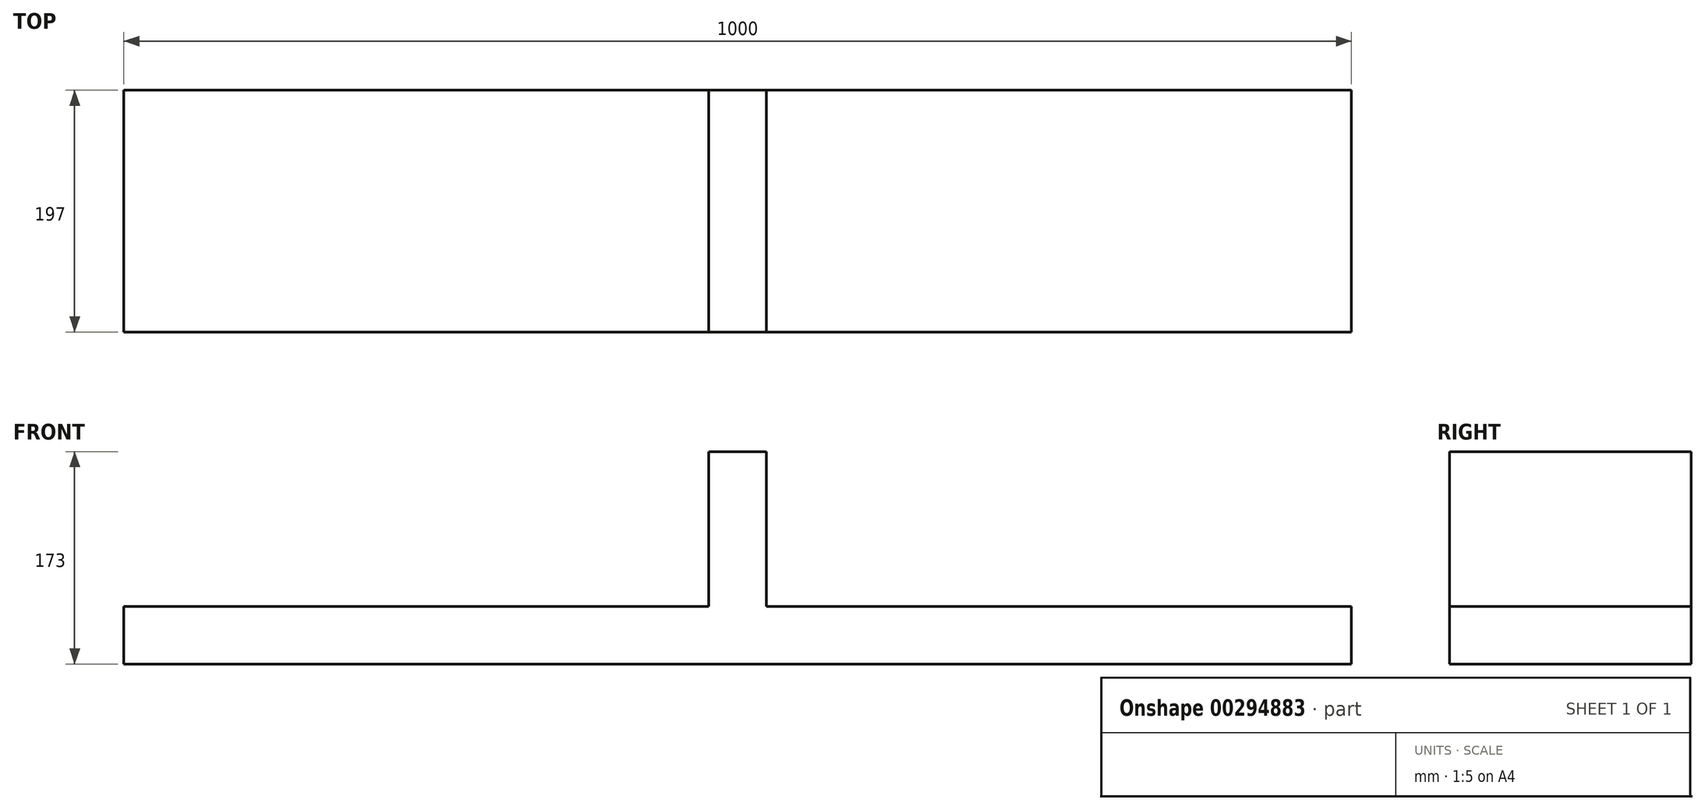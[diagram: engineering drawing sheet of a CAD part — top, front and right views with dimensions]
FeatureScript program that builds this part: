
annotation { "Feature Type Name" : "Feature", "Feature Type Description" : "" }
export const myFeature = defineFeature(function(context is Context, id is Id, definition is map)
    precondition{}
    {
        {
            var Q0;
            Q0=qCreatedBy(makeId("Front.planeOp"),FACE);
            var sketch = newSketch(context, id + "F0", { "sketchPlane" : qUnion([Q0])});
            skLineSegment(sketch, "E0", {"start": v(0, 173) * mm, "end": v(0, 0) * mm, "construction": true});
            skLineSegment(sketch, "E1", {"start": v(0, 0) * mm, "end": v(500, 0) * mm});
            skLineSegment(sketch, "E2", {"start": v(500, 0) * mm, "end": v(500, 47) * mm});
            skLineSegment(sketch, "E3", {"start": v(500, 47) * mm, "end": v(23.5, 47) * mm});
            skLineSegment(sketch, "E4", {"start": v(23.5, 47) * mm, "end": v(23.5, 173) * mm});
            skLineSegment(sketch, "E5", {"start": v(23.5, 173) * mm, "end": v(0, 173) * mm});
            skLineSegment(sketch, "E6.MirrorCS", {"start": v(-23.5, 173) * mm, "end": v(0, 173) * mm});
            skLineSegment(sketch, "E7.MirrorCS", {"start": v(-23.5, 47) * mm, "end": v(-23.5, 173) * mm});
            skLineSegment(sketch, "E8.MirrorCS", {"start": v(-500, 47) * mm, "end": v(-23.5, 47) * mm});
            skLineSegment(sketch, "E9.MirrorCS", {"start": v(-500, 0) * mm, "end": v(-500, 47) * mm});
            skLineSegment(sketch, "E10.MirrorCS", {"start": v(0, 0) * mm, "end": v(-500, 0) * mm});
            skSolve(sketch);
        }
        {
            var Q0;
            Q0 = qSketchRegion(id + "F0", true);
            extrude(context, id + "F1", {"entities" : qUnion([Q0]), "depth" : 197 * mm});
        }
    });
